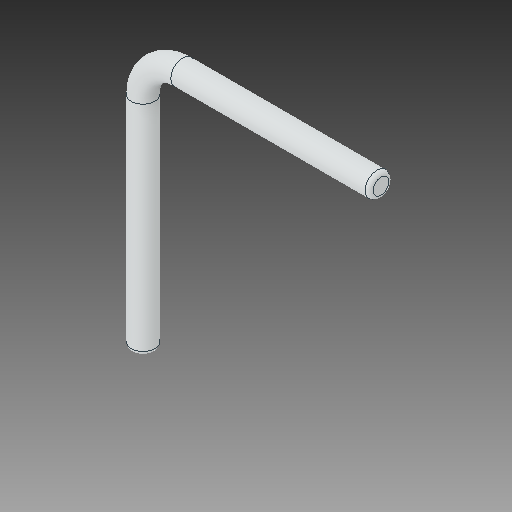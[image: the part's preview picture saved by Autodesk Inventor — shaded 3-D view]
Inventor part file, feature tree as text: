
AUTODESK INVENTOR PART (.ipt)
format: ipt  version: 2019 (Build 230136000, 136)  size: 99,840 bytes
history: mixed  units: mm
features: other x1, fillet x1, imported_body x1
ambient origin geometry x8: Origin, YZ Plane, XZ Plane, XY Plane, X Axis, Y Axis, Z Axis, Center Point
bodies: Body1 (imported_parasolid)
feature tree (3):
  other  "Твердое тело1"
  fillet  "Fillet1"  [1 undecoded]
  imported_body  NMx_Import_Brep_tag  [imported B-rep: ~7 faces, bbox_mm=[6.0, 6.8, 0.3]]
note: 1 required parameter value undecoded (feature->parameter linkage not recoverable at this tier; creation-order binding heuristic only, values carry confidence <= 0.55)
